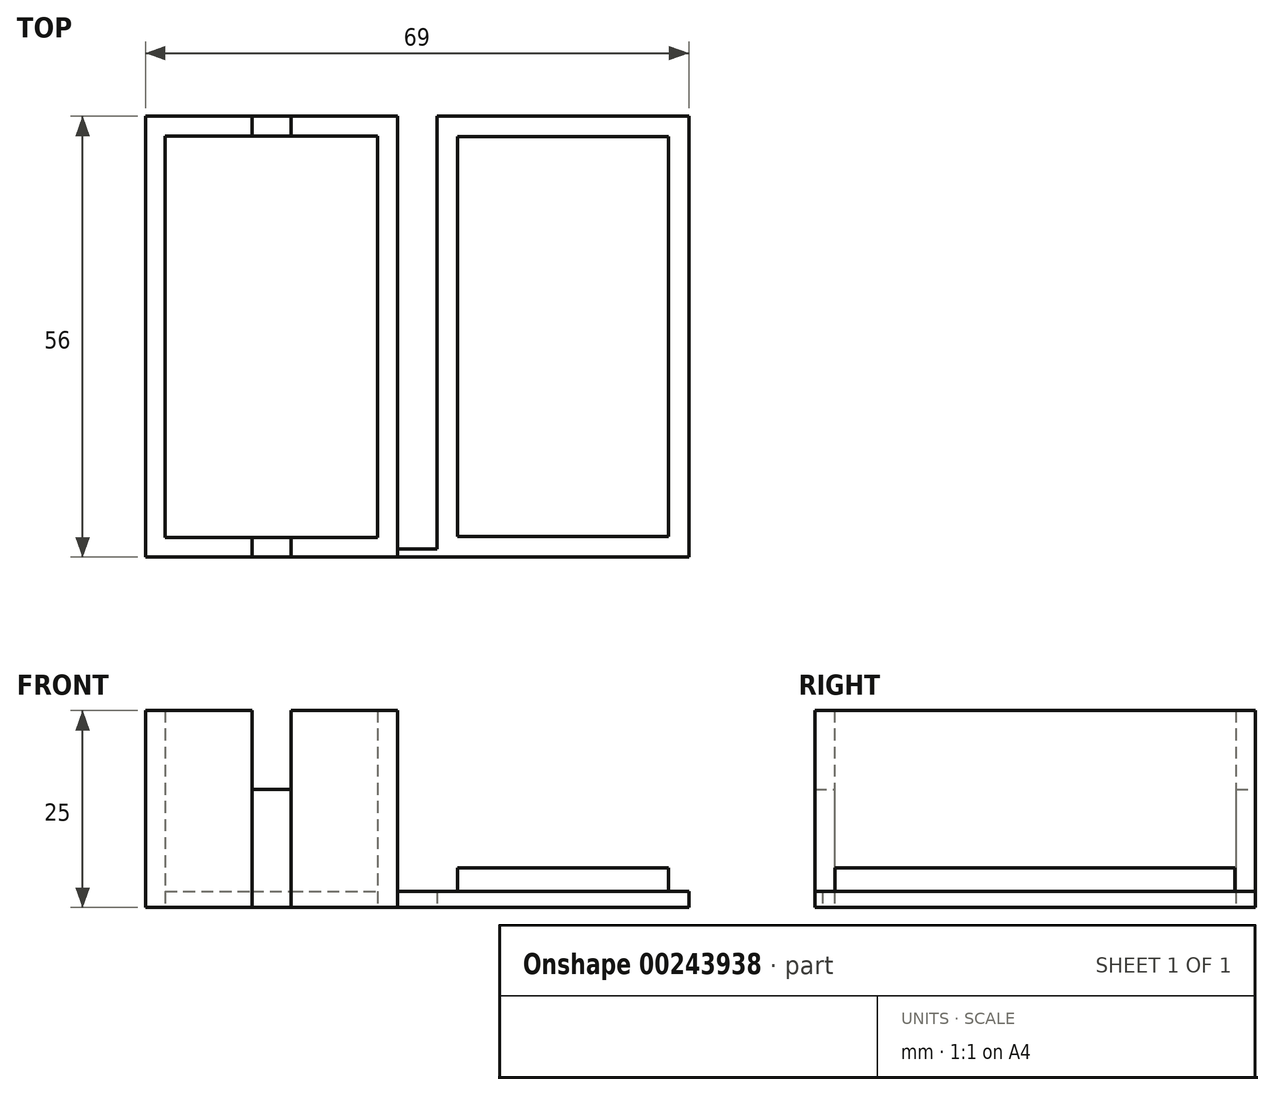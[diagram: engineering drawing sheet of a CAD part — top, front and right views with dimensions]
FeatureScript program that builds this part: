
annotation { "Feature Type Name" : "Feature", "Feature Type Description" : "" }
export const myFeature = defineFeature(function(context is Context, id is Id, definition is map)
    precondition{}
    {
        {
            var Q0;
            Q0=qCreatedBy(makeId("Top.planeOp"),FACE);
            var sketch = newSketch(context, id + "F0", { "sketchPlane" : qUnion([Q0])});
            skLineSegment(sketch, "E0.bottom", {"start": v(0, 0) * mm, "end": v(32, 0) * mm});
            skLineSegment(sketch, "E0.top", {"start": v(0, 56) * mm, "end": v(32, 56) * mm});
            skLineSegment(sketch, "E0.left", {"start": v(0, 0) * mm, "end": v(0, 56) * mm});
            skLineSegment(sketch, "E0.right", {"start": v(32, 0) * mm, "end": v(32, 56) * mm});
            skLineSegment(sketch, "E1.0", {"start": v(2.5, 2.5) * mm, "end": v(2.5, 53.5) * mm});
            skLineSegment(sketch, "E2.0", {"start": v(29.5, 2.5) * mm, "end": v(29.5, 53.5) * mm});
            skLineSegment(sketch, "E3.0", {"start": v(2.5, 2.5) * mm, "end": v(29.5, 2.5) * mm});
            skLineSegment(sketch, "E4.0", {"start": v(2.5, 53.5) * mm, "end": v(29.5, 53.5) * mm});
            skLineSegment(sketch, "E5", {"start": v(32, 0) * mm, "end": v(37, 0) * mm});
            skLineSegment(sketch, "E6.0", {"start": v(32, 1) * mm, "end": v(37, 1) * mm});
            skLineSegment(sketch, "E7.bottom", {"start": v(37, 0) * mm, "end": v(69, 0) * mm});
            skLineSegment(sketch, "E7.top", {"start": v(37, 56) * mm, "end": v(69, 56) * mm});
            skLineSegment(sketch, "E7.left", {"start": v(37, 0) * mm, "end": v(37, 56) * mm});
            skLineSegment(sketch, "E7.right", {"start": v(69, 0) * mm, "end": v(69, 56) * mm});
            skLineSegment(sketch, "E8.0", {"start": v(39.6, 2.6) * mm, "end": v(39.6, 53.4) * mm});
            skLineSegment(sketch, "E9.0", {"start": v(66.4, 2.6) * mm, "end": v(66.4, 53.4) * mm});
            skLineSegment(sketch, "E10.0", {"start": v(39.6, 2.6) * mm, "end": v(66.4, 2.6) * mm});
            skLineSegment(sketch, "E11.0", {"start": v(39.6, 53.4) * mm, "end": v(66.4, 53.4) * mm});
            skLineSegment(sketch, "E12.0", {"start": v(18.5, 0) * mm, "end": v(18.5, 2.5) * mm});
            skLineSegment(sketch, "E13.0", {"start": v(13.5, 0) * mm, "end": v(13.5, 2.5) * mm});
            skLineSegment(sketch, "E14.trimOffspring", {"start": v(18.5, 53.5) * mm, "end": v(18.5, 56) * mm});
            skLineSegment(sketch, "E15.trimOffspring", {"start": v(13.5, 53.5) * mm, "end": v(13.5, 56) * mm});
            skSolve(sketch);
        }
        {
            var Q0;
            {var subQ3=sQuery(id+"F0.wireOp",EDGE,"E1.0");Q0=makeQuery(id+"F0.imprint","IMPRINT",FACE,{"disambiguationData":[TD([[makeQuery(id+"F0.imprint","IMPRINT",EDGE,{"derivedFrom":subQ3}),-1.0]])]});}
            var Q1;
            {var subQ0=sQuery(id+"F0.wireOp",EDGE,"E5");Q1=makeQuery(id+"F0.imprint","IMPRINT",FACE,{"disambiguationData":[TD([[makeQuery(id+"F0.imprint","IMPRINT",EDGE,{"derivedFrom":subQ0}),1.0]])]});}
            var Q2;
            {var subQ3=sQuery(id+"F0.wireOp",EDGE,"E7.bottom");Q2=makeQuery(id+"F0.imprint","IMPRINT",FACE,{"disambiguationData":[TD([[makeQuery(id+"F0.imprint","IMPRINT",EDGE,{"derivedFrom":subQ3}),1.0]])]});}
            extrude(context, id + "F1", {"entities" : qUnion([Q0, Q1, Q2]), "depth" : 2 * mm, "offsetDistance" : 25 * mm});
        }
        {
            var Q0;
            Q0=makeQuery(id+"F0.imprint","IMPRINT",FACE,{"disambiguationData":[TD([[makeQuery(id+"F0.imprint","IMPRINT",EDGE,{"derivedFrom":sQuery(id+"F0.wireOp",EDGE,"E8.0")}),-1.0]])]});
            extrude(context, id + "F2", {"entities" : qUnion([Q0]), "operationType" : NewBodyOperationType.ADD, "depth" : 5 * mm, "offsetDistance" : 25 * mm});
        }
        {
            var Q0;
            {var subQ0=sQuery(id+"F0.wireOp",EDGE,"E12.0");Q0=makeQuery(id+"F0.imprint","IMPRINT",FACE,{"disambiguationData":[TD([[makeQuery(id+"F0.imprint","IMPRINT",EDGE,{"derivedFrom":subQ0}),1.0]])]});}
            var Q1;
            {var subQ0=sQuery(id+"F0.wireOp",EDGE,"E14.trimOffspring");Q1=makeQuery(id+"F0.imprint","IMPRINT",FACE,{"disambiguationData":[TD([[makeQuery(id+"F0.imprint","IMPRINT",EDGE,{"derivedFrom":subQ0}),1.0]])]});}
            extrude(context, id + "F3", {"entities" : qUnion([Q0, Q1]), "operationType" : NewBodyOperationType.ADD, "depth" : 15 * mm, "offsetDistance" : 25 * mm});
        }
        {
            var Q0;
            {var subQ2=sQuery(id+"F0.wireOp",EDGE,"E0.left");Q0=makeQuery(id+"F0.imprint","IMPRINT",FACE,{"disambiguationData":[TD([[makeQuery(id+"F0.imprint","IMPRINT",EDGE,{"derivedFrom":subQ2}),-1.0]])]});}
            var Q1;
            {var subQ6=sQuery(id+"F0.wireOp",EDGE,"E2.0");Q1=makeQuery(id+"F0.imprint","IMPRINT",FACE,{"disambiguationData":[TD([[makeQuery(id+"F0.imprint","IMPRINT",EDGE,{"derivedFrom":subQ6}),-1.0]])]});}
            extrude(context, id + "F4", {"entities" : qUnion([Q0, Q1]), "depth" : 25 * mm, "offsetDistance" : 25 * mm});
        }
    });
